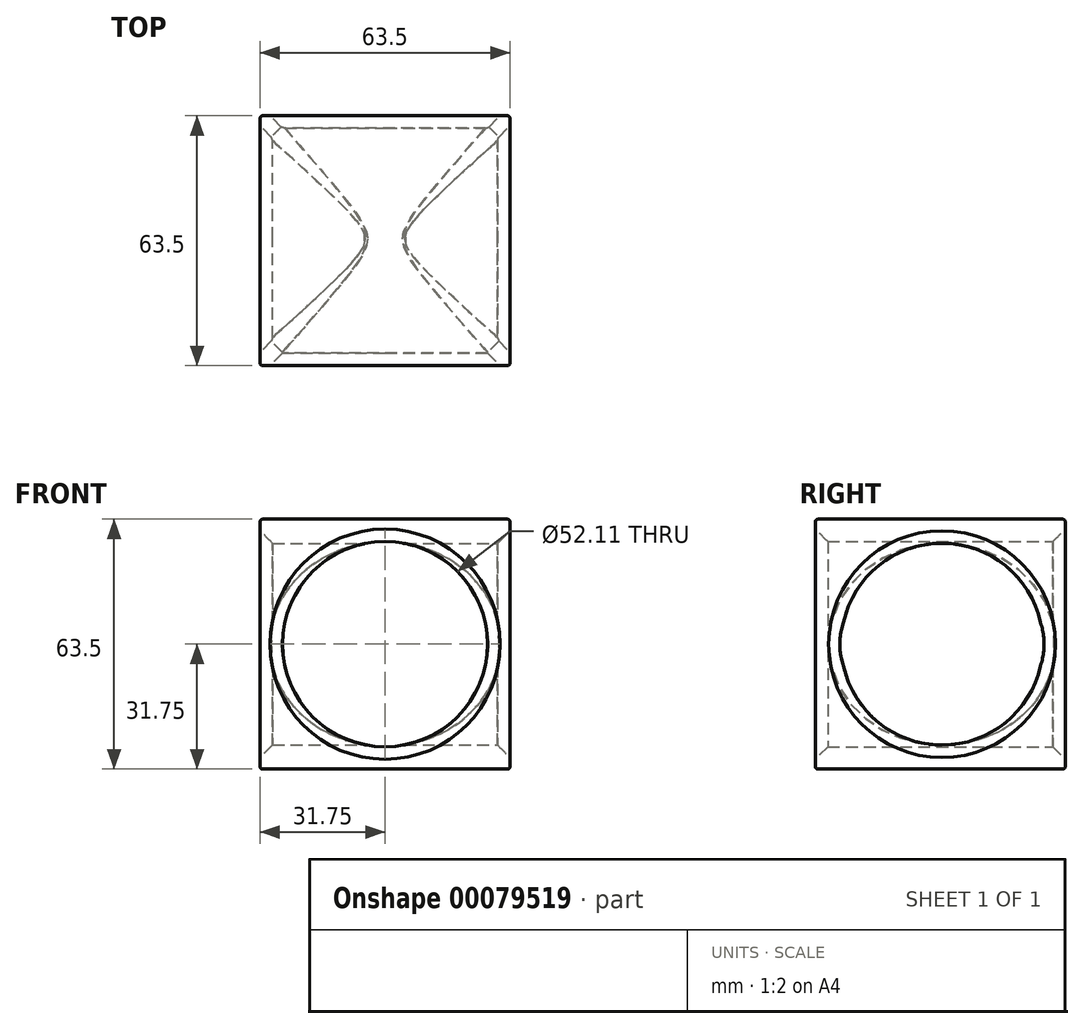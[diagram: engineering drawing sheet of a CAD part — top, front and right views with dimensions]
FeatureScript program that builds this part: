
annotation { "Feature Type Name" : "Feature", "Feature Type Description" : "" }
export const myFeature = defineFeature(function(context is Context, id is Id, definition is map)
    precondition{}
    {
        {
            var Q0;
            Q0=qCreatedBy(makeId("Top.planeOp"),FACE);
            var sketch = newSketch(context, id + "F0", { "sketchPlane" : qUnion([Q0])});
            skLineSegment(sketch, "E0", {"start": v(0, 0) * mm, "end": v(63.5, 0) * mm});
            skLineSegment(sketch, "E1", {"start": v(0, 0) * mm, "end": v(0, 63.5) * mm});
            skLineSegment(sketch, "E2", {"start": v(0, 63.5) * mm, "end": v(63.5, 63.5) * mm});
            skLineSegment(sketch, "E3", {"start": v(63.5, 63.5) * mm, "end": v(63.5, 0) * mm});
            skSolve(sketch);
        }
        {
            var Q0;
            Q0 = qSketchRegion(id + "F0", true);
            extrude(context, id + "F1", {"entities" : qUnion([Q0]), "depth" : 63.5 * mm});
        }
        {
            var Q0;
            Q0=makeQuery(id+"F1.opExtrude","SWEPT_FACE",FACE,{"disambiguationData":[OSD([sQuery(id+"F0.wireOp",EDGE,"E3")])]});
            var sketch = newSketch(context, id + "F2", { "sketchPlane" : qUnion([Q0])});
            skLineSegment(sketch, "E4", {"start": v(31.75, 63.5) * mm, "end": v(32.6, 0) * mm});
            skCircle(sketch, "E5", {"center": v(32.18, 31.75) * mm, "radius": 25.62 * mm});
            skSolve(sketch);
        }
        {
            var Q0;
            {var subQ0=sQuery(id+"F2.wireOp",EDGE,"E5");var subQ1=sQuery(id+"F2.wireOp",EDGE,"E4");var subQ2=makeQuery(id+"F2.imprint","INTERSECT",VERTEX,{"disambiguationData":[OD(0.0)],"derivedFrom":[subQ1,subQ0]});Q0=makeQuery(id+"F2.imprint","IMPRINT",FACE,{"disambiguationData":[TD([[makeQuery(id+"F2.imprint","IMPRINT",EDGE,{"disambiguationData":[TD([[subQ2,-1.0]])],"derivedFrom":subQ1}),-1.0]])]});}
            var Q1;
            {var subQ0=sQuery(id+"F2.wireOp",EDGE,"E5");var subQ1=sQuery(id+"F2.wireOp",EDGE,"E4");var subQ2=makeQuery(id+"F2.imprint","INTERSECT",VERTEX,{"disambiguationData":[OD(0.0)],"derivedFrom":[subQ1,subQ0]});Q1=makeQuery(id+"F2.imprint","IMPRINT",FACE,{"disambiguationData":[TD([[makeQuery(id+"F2.imprint","IMPRINT",EDGE,{"disambiguationData":[TD([[subQ2,-1.0]])],"derivedFrom":subQ1}),1.0]])]});}
            extrude(context, id + "F3", {"entities" : qUnion([Q0, Q1]), "operationType" : NewBodyOperationType.REMOVE, "oppositeDirection" : true, "depth" : 63.5 * mm});
        }
        {
            var Q0;
            Q0=makeQuery(id+"F1.opExtrude","SWEPT_FACE",FACE,{"disambiguationData":[OSD([sQuery(id+"F0.wireOp",EDGE,"E2")])]});
            var sketch = newSketch(context, id + "F4", { "sketchPlane" : qUnion([Q0])});
            skLineSegment(sketch, "E6", {"start": v(-31.75, 63.5) * mm, "end": v(-31.75, 0) * mm});
            skCircle(sketch, "E7", {"center": v(-31.75, 31.75) * mm, "radius": 26.05 * mm});
            skSolve(sketch);
        }
        {
            var Q0;
            Q0 = qSketchRegion(id + "F4", true);
            extrude(context, id + "F5", {"entities" : qUnion([Q0]), "operationType" : NewBodyOperationType.REMOVE, "oppositeDirection" : true, "depth" : 63.5 * mm});
        }
        {
            var Q0;
            Q0=makeQuery(id+"F5.boolean.opBoolean","SPLIT",FACE,{"disambiguationData":[TD([makeQuery(id+"F1.opExtrude","SWEPT_FACE",FACE,{"disambiguationData":[OSD([sQuery(id+"F0.wireOp",EDGE,"E3")])]})])],"derivedFrom":makeQuery(id+"F3.boolean.opBoolean","COPY",FACE,{"derivedFrom":makeQuery(id+"F3.opExtrude","SWEPT_FACE",FACE,{"disambiguationData":[OSD([sQuery(id+"F2.wireOp",EDGE,"E5")])]})})});
            var Q1;
            Q1=makeQuery(id+"F5.boolean.opBoolean","COPY",FACE,{"derivedFrom":makeQuery(id+"F5.opExtrude","SWEPT_FACE",FACE,{"disambiguationData":[OSD([sQuery(id+"F4.wireOp",EDGE,"E7")])]})});
            var Q2;
            Q2=makeQuery(id+"F5.boolean.opBoolean","SPLIT",FACE,{"disambiguationData":[TD([makeQuery(id+"F1.opExtrude","SWEPT_FACE",FACE,{"disambiguationData":[OSD([sQuery(id+"F0.wireOp",EDGE,"E1")])]})])],"derivedFrom":makeQuery(id+"F3.boolean.opBoolean","COPY",FACE,{"derivedFrom":makeQuery(id+"F3.opExtrude","SWEPT_FACE",FACE,{"disambiguationData":[OSD([sQuery(id+"F2.wireOp",EDGE,"E5")])]})})});
            chamfer(context, id + "F6", {"entities" : qUnion([Q0, Q1, Q2]), "width" : 3.17 * mm, "tangentPropagation" : true});
        }
        {
            var Q0;
            Q0=makeQuery(id+"F1.opExtrude","SWEPT_EDGE",EDGE,{"disambiguationData":[OSD([sQuery(id+"F0.wireOp",EDGE,"E0"),sQuery(id+"F0.wireOp",EDGE,"E3")])]});
            var Q1;
            Q1=makeQuery(id+"F1.opExtrude","CAP_EDGE",EDGE,{"disambiguationData":[OSD([sQuery(id+"F0.wireOp",EDGE,"E0")])],"isStart":false});
            var Q2;
            Q2=makeQuery(id+"F1.opExtrude","CAP_EDGE",EDGE,{"disambiguationData":[OSD([sQuery(id+"F0.wireOp",EDGE,"E3")])],"isStart":false});
            var Q3;
            Q3=makeQuery(id+"F1.opExtrude","CAP_EDGE",EDGE,{"disambiguationData":[OSD([sQuery(id+"F0.wireOp",EDGE,"E2")])],"isStart":false});
            var Q4;
            Q4=makeQuery(id+"F1.opExtrude","CAP_EDGE",EDGE,{"disambiguationData":[OSD([sQuery(id+"F0.wireOp",EDGE,"E3")])],"isStart":true});
            var Q5;
            Q5=makeQuery(id+"F1.opExtrude","CAP_EDGE",EDGE,{"disambiguationData":[OSD([sQuery(id+"F0.wireOp",EDGE,"E0")])],"isStart":true});
            var Q6;
            Q6=makeQuery(id+"F1.opExtrude","SWEPT_EDGE",EDGE,{"disambiguationData":[OSD([sQuery(id+"F0.wireOp",EDGE,"E0"),sQuery(id+"F0.wireOp",EDGE,"E1")])]});
            var Q7;
            Q7=makeQuery(id+"F1.opExtrude","CAP_EDGE",EDGE,{"disambiguationData":[OSD([sQuery(id+"F0.wireOp",EDGE,"E1")])],"isStart":true});
            var Q8;
            Q8=makeQuery(id+"F1.opExtrude","CAP_EDGE",EDGE,{"disambiguationData":[OSD([sQuery(id+"F0.wireOp",EDGE,"E1")])],"isStart":false});
            var Q9;
            Q9=makeQuery(id+"F1.opExtrude","SWEPT_EDGE",EDGE,{"disambiguationData":[OSD([sQuery(id+"F0.wireOp",EDGE,"E1"),sQuery(id+"F0.wireOp",EDGE,"E2")])]});
            var Q10;
            Q10=makeQuery(id+"F1.opExtrude","CAP_EDGE",EDGE,{"disambiguationData":[OSD([sQuery(id+"F0.wireOp",EDGE,"E2")])],"isStart":true});
            var Q11;
            Q11=makeQuery(id+"F1.opExtrude","SWEPT_EDGE",EDGE,{"disambiguationData":[OSD([sQuery(id+"F0.wireOp",EDGE,"E2"),sQuery(id+"F0.wireOp",EDGE,"E3")])]});
            fillet(context, id + "F7", {"entities" : qUnion([Q0, Q1, Q2, Q3, Q4, Q5, Q6, Q7, Q8, Q9, Q10, Q11]), "radius" : 0.67 * mm, "tangentPropagation" : true, "allowEdgeOverflow" : false});
        }
    });
